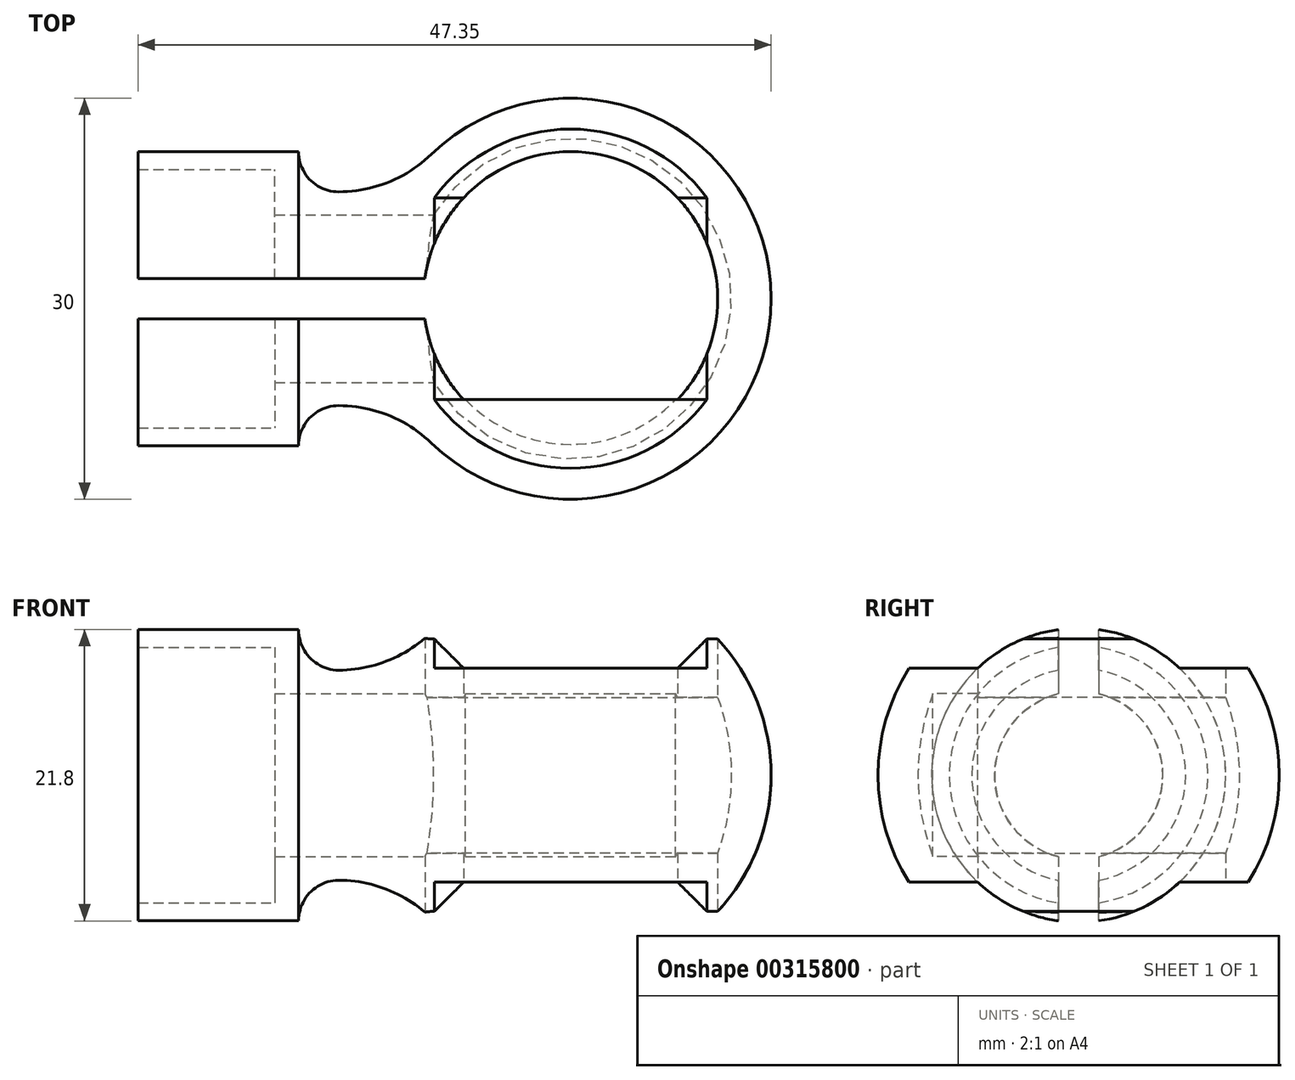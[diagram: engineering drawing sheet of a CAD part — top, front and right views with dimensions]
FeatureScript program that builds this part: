
annotation { "Feature Type Name" : "Feature", "Feature Type Description" : "" }
export const myFeature = defineFeature(function(context is Context, id is Id, definition is map)
    precondition{}
    {
        {
            var Q0;
            Q0=qCreatedBy(makeId("Front.planeOp"),FACE);
            var sketch = newSketch(context, id + "F0", { "sketchPlane" : qUnion([Q0])});
            skLineSegment(sketch, "E0", {"start": v(26.1, 0.44) * mm, "end": v(-21.26, 0.44) * mm});
            skLineSegment(sketch, "E1", {"start": v(-21.26, 10.11) * mm, "end": v(-21.26, 11.44) * mm});
            skLineSegment(sketch, "E2", {"start": v(-21.26, 11.44) * mm, "end": v(-9.26, 11.44) * mm});
            skLineSegment(sketch, "E3", {"start": v(-9.26, 11.44) * mm, "end": v(-9.26, 8.44) * mm});
            skLineSegment(sketch, "E4", {"start": v(-9.26, 8.44) * mm, "end": v(-6.26, 8.44) * mm});
            skArc(sketch, "E5", {"start": v(-6.26, 8.44) * mm, "mid": v(-2.52, 9.17) * mm, "end": v(0.68, 11.24) * mm});
            skArc(sketch, "E6", {"start": v(26.1, 0.44) * mm, "mid": v(16.96, 14.25) * mm, "end": v(0.68, 11.24) * mm});
            skLineSegment(sketch, "E7", {"start": v(-21.26, 10.11) * mm, "end": v(-11.03, 10.11) * mm});
            skLineSegment(sketch, "E8", {"start": v(-11.03, 10.11) * mm, "end": v(-11.03, 6.72) * mm});
            skLineSegment(sketch, "E9", {"start": v(-11.03, 6.72) * mm, "end": v(4.52, 6.72) * mm});
            skLineSegment(sketch, "E10", {"start": v(4.52, 6.72) * mm, "end": v(4.52, 0.44) * mm});
            skSolve(sketch);
        }
        {
            var Q0;
            Q0=makeQuery(id+"F0.imprint","IMPRINT",FACE,{"disambiguationData":[TD([[makeQuery(id+"F0.imprint","IMPRINT",EDGE,{"derivedFrom":sQuery(id+"F0.wireOp",EDGE,"E0")}),-1.0]])]});
            var Q1;
            Q1=sQuery(id+"F0.wireOp",EDGE,"E0");
            revolve(context, id + "F1", {"entities" : qUnion([Q0]), "axis" : qUnion([Q1]), "revolveType" : RevolveType.FULL});
        }
        {
            var Q0;
            Q0=makeQuery(id+"F1.opRevolve","SWEPT_FACE",FACE,{"disambiguationData":[OSD([sQuery(id+"F0.wireOp",EDGE,"E3")])]});
            var sketch = newSketch(context, id + "F2", { "sketchPlane" : qUnion([Q0])});
            skLineSegment(sketch, "E11.bottom", {"start": v(33.24, -7.56) * mm, "end": v(-33.24, -7.56) * mm});
            skLineSegment(sketch, "E11.top", {"start": v(33.24, 8.44) * mm, "end": v(-33.24, 8.44) * mm});
            skLineSegment(sketch, "E11.left", {"start": v(33.24, -7.56) * mm, "end": v(33.24, 8.44) * mm});
            skLineSegment(sketch, "E11.right", {"start": v(-33.24, -7.56) * mm, "end": v(-33.24, 8.44) * mm});
            skPoint(sketch, "E11.middle", {"position": v(0, 0.44) * mm});
            skCircle(sketch, "E12.0", {"center": v(0, 0.44) * mm, "radius": 8 * mm});
            skLineSegment(sketch, "E13.bottom", {"start": v(33.24, -7.56) * mm, "end": v(-36.84, -7.56) * mm});
            skLineSegment(sketch, "E13.top", {"start": v(33.24, -24.97) * mm, "end": v(-36.84, -24.97) * mm});
            skLineSegment(sketch, "E13.left", {"start": v(33.24, -7.56) * mm, "end": v(33.24, -24.97) * mm});
            skLineSegment(sketch, "E13.right", {"start": v(-36.84, -7.56) * mm, "end": v(-36.84, -24.97) * mm});
            skLineSegment(sketch, "E14.bottom", {"start": v(33.24, 8.44) * mm, "end": v(-51.44, 8.44) * mm});
            skLineSegment(sketch, "E14.top", {"start": v(33.24, 29.21) * mm, "end": v(-51.44, 29.21) * mm});
            skLineSegment(sketch, "E14.left", {"start": v(33.24, 8.44) * mm, "end": v(33.24, 29.21) * mm});
            skLineSegment(sketch, "E14.right", {"start": v(-51.44, 8.44) * mm, "end": v(-51.44, 29.21) * mm});
            skSolve(sketch);
        }
        {
            var Q0;
            Q0=makeQuery(id+"F2.imprint","IMPRINT",FACE,{"disambiguationData":[TD([[makeQuery(id+"F2.imprint","IMPRINT",EDGE,{"derivedFrom":sQuery(id+"F2.wireOp",EDGE,"E13.top")}),-1.0]])]});
            var Q1;
            Q1=makeQuery(id+"F2.imprint","IMPRINT",FACE,{"disambiguationData":[TD([[makeQuery(id+"F2.imprint","IMPRINT",EDGE,{"derivedFrom":sQuery(id+"F2.wireOp",EDGE,"E14.top")}),1.0]])]});
            var Q2;
            {var subQ0=sQuery(id+"F2.wireOp",EDGE,"E13.bottom");var subQ1=makeQuery(id+"F2.imprint","INTERSECT",VERTEX,{"derivedFrom":[sQuery(id+"F2.wireOp",EDGE,"E12.0"),subQ0]});Q2=makeQuery(id+"F2.imprint","IMPRINT",FACE,{"disambiguationData":[TD([[makeQuery(id+"F2.imprint","IMPRINT",EDGE,{"disambiguationData":[TD([[subQ1,1.0]])],"derivedFrom":subQ0}),1.0]])]});}
            var Q3;
            {var subQ0=sQuery(id+"F2.wireOp",EDGE,"E14.bottom");var subQ1=makeQuery(id+"F2.imprint","INTERSECT",VERTEX,{"derivedFrom":[sQuery(id+"F2.wireOp",EDGE,"E12.0"),subQ0]});Q3=makeQuery(id+"F2.imprint","IMPRINT",FACE,{"disambiguationData":[TD([[makeQuery(id+"F2.imprint","IMPRINT",EDGE,{"disambiguationData":[TD([[subQ1,1.0]])],"derivedFrom":subQ0}),-1.0]])]});}
            extrude(context, id + "F3", {"entities" : qUnion([Q0, Q1, Q2, Q3]), "operationType" : NewBodyOperationType.REMOVE, "endBound" : BoundingType.THROUGH_ALL, "depth" : 25 * mm, "offsetDistance" : 25 * mm});
        }
        {
            var Q0;
            Q0=makeQuery(id+"F3.boolean.opBoolean","COPY",FACE,{"derivedFrom":makeQuery(id+"F3.opExtrude","SWEPT_FACE",FACE,{"disambiguationData":[OSD([sQuery(id+"F2.wireOp",EDGE,"E13.bottom")])]})});
            var sketch = newSketch(context, id + "F4", { "sketchPlane" : qUnion([Q0])});
            skArc(sketch, "E15", {"start": v(0.2, -1.5) * mm, "mid": v(22.1, 0) * mm, "end": v(0.2, 1.5) * mm});
            skLineSegment(sketch, "E16.bottom", {"start": v(-32, 1.5) * mm, "end": v(0.2, 1.5) * mm});
            skLineSegment(sketch, "E16.top", {"start": v(-32, -1.5) * mm, "end": v(0.2, -1.5) * mm});
            skLineSegment(sketch, "E16.left", {"start": v(-32, 1.5) * mm, "end": v(-32, -1.5) * mm});
            skLineSegment(sketch, "E16.right", {"start": v(54.18, 1.5) * mm, "end": v(54.18, -1.5) * mm});
            skSolve(sketch);
        }
        {
            var Q0;
            {var subQ8=sQuery(id+"F4.wireOp",EDGE,"E15");Q0=makeQuery(id+"F4.imprint","IMPRINT",FACE,{"disambiguationData":[TD([[makeQuery(id+"F4.imprint","IMPRINT",EDGE,{"derivedFrom":subQ8}),1.0]])]});}
            var Q1;
            {var subQ0=sQuery(id+"F4.wireOp",EDGE,"E16.left");Q1=makeQuery(id+"F4.imprint","IMPRINT",FACE,{"disambiguationData":[TD([[makeQuery(id+"F4.imprint","IMPRINT",EDGE,{"derivedFrom":subQ0}),1.0]])]});}
            extrude(context, id + "F5", {"entities" : qUnion([Q0, Q1]), "operationType" : NewBodyOperationType.REMOVE, "endBound" : BoundingType.SYMMETRIC, "oppositeDirection" : true, "depth" : 40 * mm, "offsetDistance" : 25 * mm});
        }
        {
            var Q0;
            Q0=qCreatedBy(makeId("Front.planeOp"),FACE);
            var sketch = newSketch(context, id + "F6", { "sketchPlane" : qUnion([Q0])});
            skLineSegment(sketch, "E17.0", {"start": v(0.2, 8.44) * mm, "end": v(22.1, 8.44) * mm});
            skLineSegment(sketch, "E18.0", {"start": v(0.2, -7.56) * mm, "end": v(22.1, -7.56) * mm});
            skLineSegment(sketch, "E19", {"start": v(11.14, 0.44) * mm, "end": v(23.62, 0.44) * mm});
            skLineSegment(sketch, "E20", {"start": v(22.1, 8.44) * mm, "end": v(22.1, -7.56) * mm});
            skArc(sketch, "E21", {"start": v(22.1, -5.21) * mm, "mid": v(23.62, 0.53) * mm, "end": v(22.1, 6.28) * mm});
            skLineSegment(sketch, "E22", {"start": v(22.1, 6.28) * mm, "end": v(22.1, -5.21) * mm});
            skLineSegment(sketch, "E23", {"start": v(11.1, -7.56) * mm, "end": v(11.1, 8.44) * mm});
            skPoint(sketch, "E24.0", {"position": v(0.2, 6.54) * mm});
            skPoint(sketch, "E25.0", {"position": v(0.2, -5.66) * mm});
            skArc(sketch, "E26", {"start": v(0.2, 6.54) * mm, "mid": v(-0.92, 0.44) * mm, "end": v(0.2, -5.66) * mm});
            skLineSegment(sketch, "E27", {"start": v(0.2, 6.54) * mm, "end": v(0.2, -5.66) * mm});
            skSolve(sketch);
        }
        {
            var Q0;
            Q0=makeQuery(id+"F6.imprint","IMPRINT",FACE,{"disambiguationData":[TD([[makeQuery(id+"F6.imprint","IMPRINT",EDGE,{"derivedFrom":sQuery(id+"F6.wireOp",EDGE,"E26")}),1.0]])]});
            var Q1;
            Q1=sQuery(id+"F6.wireOp",EDGE,"E23");
            revolve(context, id + "F7", {"operationType" : NewBodyOperationType.REMOVE, "entities" : qUnion([Q0]), "axis" : qUnion([Q1]), "revolveType" : RevolveType.FULL, "oppositeDirection" : true});
        }
        {
            var Q0;
            {var subQ0=sQuery(id+"F0.wireOp",EDGE,"E3");var subQ1=sQuery(id+"F0.wireOp",EDGE,"E4");Q0=makeQuery(id+"F5.boolean.opBoolean","SPLIT",EDGE,{"disambiguationData":[TD([makeQuery(id+"F5.opExtrude","SWEPT_FACE",FACE,{"disambiguationData":[OSD([sQuery(id+"F4.wireOp",EDGE,"E16.bottom")])]})])],"derivedFrom":makeQuery(id+"F1.opRevolve","SWEPT_EDGE",EDGE,{"disambiguationData":[OSD([subQ0,subQ1])]})});}
            var Q1;
            {var subQ0=sQuery(id+"F0.wireOp",EDGE,"E3");var subQ1=sQuery(id+"F0.wireOp",EDGE,"E4");Q1=makeQuery(id+"F5.boolean.opBoolean","SPLIT",EDGE,{"disambiguationData":[TD([makeQuery(id+"F5.opExtrude","SWEPT_FACE",FACE,{"disambiguationData":[OSD([sQuery(id+"F4.wireOp",EDGE,"E16.top")])]})])],"derivedFrom":makeQuery(id+"F1.opRevolve","SWEPT_EDGE",EDGE,{"disambiguationData":[OSD([subQ0,subQ1])]})});}
            fillet(context, id + "F8", {"entities" : qUnion([Q0, Q1]), "radius" : 3 * mm, "tangentPropagation" : true, "allowEdgeOverflow" : false});
        }
    });
